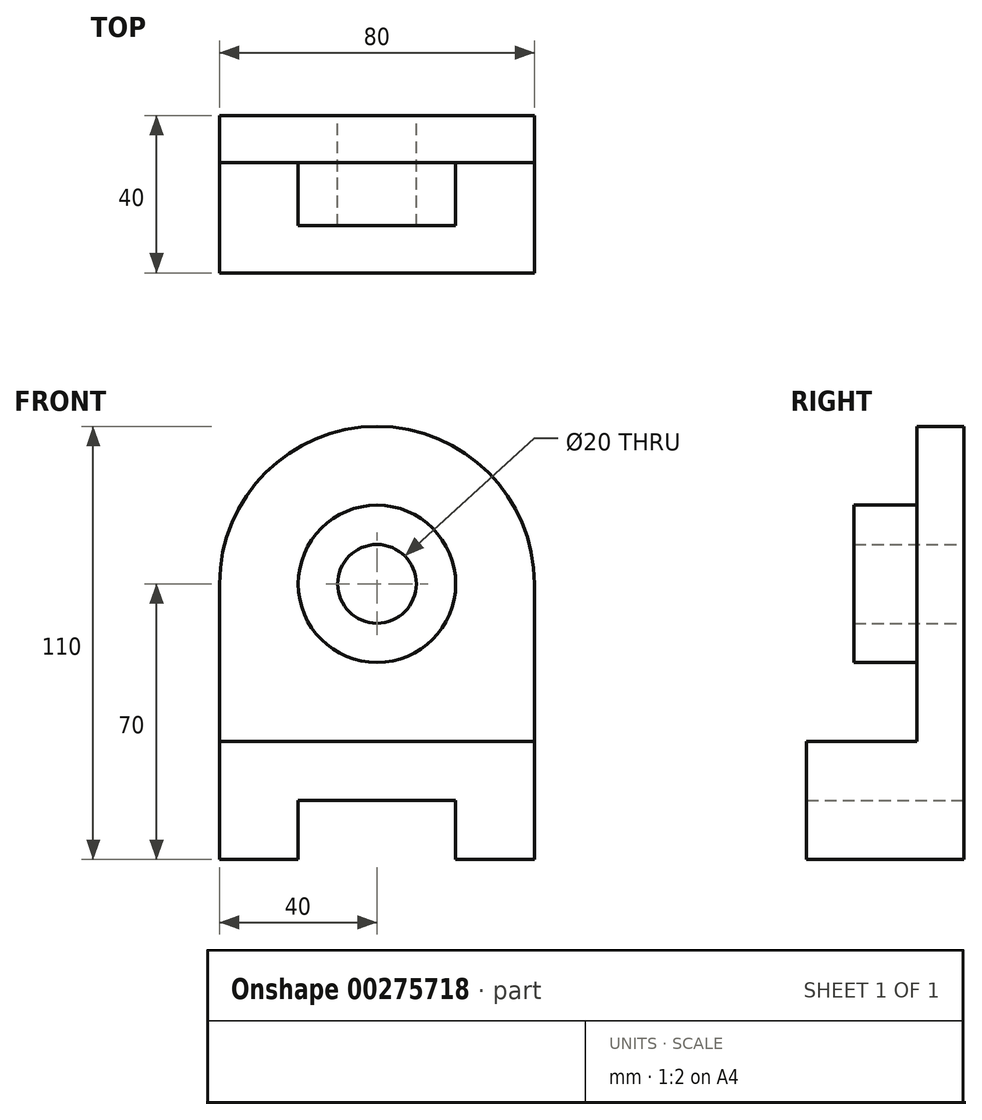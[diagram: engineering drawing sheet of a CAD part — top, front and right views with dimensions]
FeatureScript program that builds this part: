
annotation { "Feature Type Name" : "Feature", "Feature Type Description" : "" }
export const myFeature = defineFeature(function(context is Context, id is Id, definition is map)
    precondition{}
    {
        {
            var Q0;
            Q0=qCreatedBy(makeId("Front.planeOp"),FACE);
            var sketch = newSketch(context, id + "F0", { "sketchPlane" : qUnion([Q0])});
            skLineSegment(sketch, "E0.left", {"start": v(-40, 35) * mm, "end": v(-40, -35) * mm});
            skLineSegment(sketch, "E0.right", {"start": v(40, 35) * mm, "end": v(40, -35) * mm});
            skArc(sketch, "E1", {"start": v(40, 35) * mm, "mid": v(0, 75) * mm, "end": v(-40, 35) * mm});
            skCircle(sketch, "E2", {"center": v(0, 35) * mm, "radius": 20 * mm});
            skCircle(sketch, "E3", {"center": v(0, 35) * mm, "radius": 10 * mm});
            skLineSegment(sketch, "E4.left", {"start": v(-20, -20) * mm, "end": v(-20, -35) * mm});
            skLineSegment(sketch, "E4.right", {"start": v(20, -20) * mm, "end": v(20, -35) * mm});
            skLineSegment(sketch, "E5.trimOffspring", {"start": v(20, -35) * mm, "end": v(40, -35) * mm});
            skLineSegment(sketch, "E6", {"start": v(-40, -35) * mm, "end": v(-20, -35) * mm});
            skLineSegment(sketch, "E7.top", {"start": v(-40, -5) * mm, "end": v(40, -5) * mm});
            skLineSegment(sketch, "E8", {"start": v(-20, -20) * mm, "end": v(20, -20) * mm});
            skSolve(sketch);
        }
        {
            var Q0;
            Q0=makeQuery(id+"F0.imprint","IMPRINT",FACE,{"disambiguationData":[TD([[makeQuery(id+"F0.imprint","IMPRINT",EDGE,{"derivedFrom":sQuery(id+"F0.wireOp",EDGE,"E2")}),1.0]])]});
            extrude(context, id + "F1", {"entities" : qUnion([Q0]), "depth" : 28 * mm});
        }
        {
            var Q0;
            {var subQ0=sQuery(id+"F0.wireOp",EDGE,"E1");Q0=makeQuery(id+"F0.imprint","IMPRINT",FACE,{"disambiguationData":[TD([[makeQuery(id+"F0.imprint","IMPRINT",EDGE,{"derivedFrom":subQ0}),1.0]])]});}
            var Q1;
            Q1=makeQuery(id+"F0.imprint","IMPRINT",FACE,{"disambiguationData":[TD([[makeQuery(id+"F0.imprint","IMPRINT",EDGE,{"derivedFrom":sQuery(id+"F0.wireOp",EDGE,"E4.left")}),-1.0]])]});
            extrude(context, id + "F2", {"entities" : qUnion([Q0, Q1]), "operationType" : NewBodyOperationType.ADD, "depth" : 12 * mm});
        }
        {
            var Q0;
            Q0=makeQuery(id+"F0.imprint","IMPRINT",FACE,{"disambiguationData":[TD([[makeQuery(id+"F0.imprint","IMPRINT",EDGE,{"derivedFrom":sQuery(id+"F0.wireOp",EDGE,"E4.left")}),-1.0]])]});
            extrude(context, id + "F3", {"entities" : qUnion([Q0]), "operationType" : NewBodyOperationType.ADD, "depth" : 40 * mm});
        }
    });
